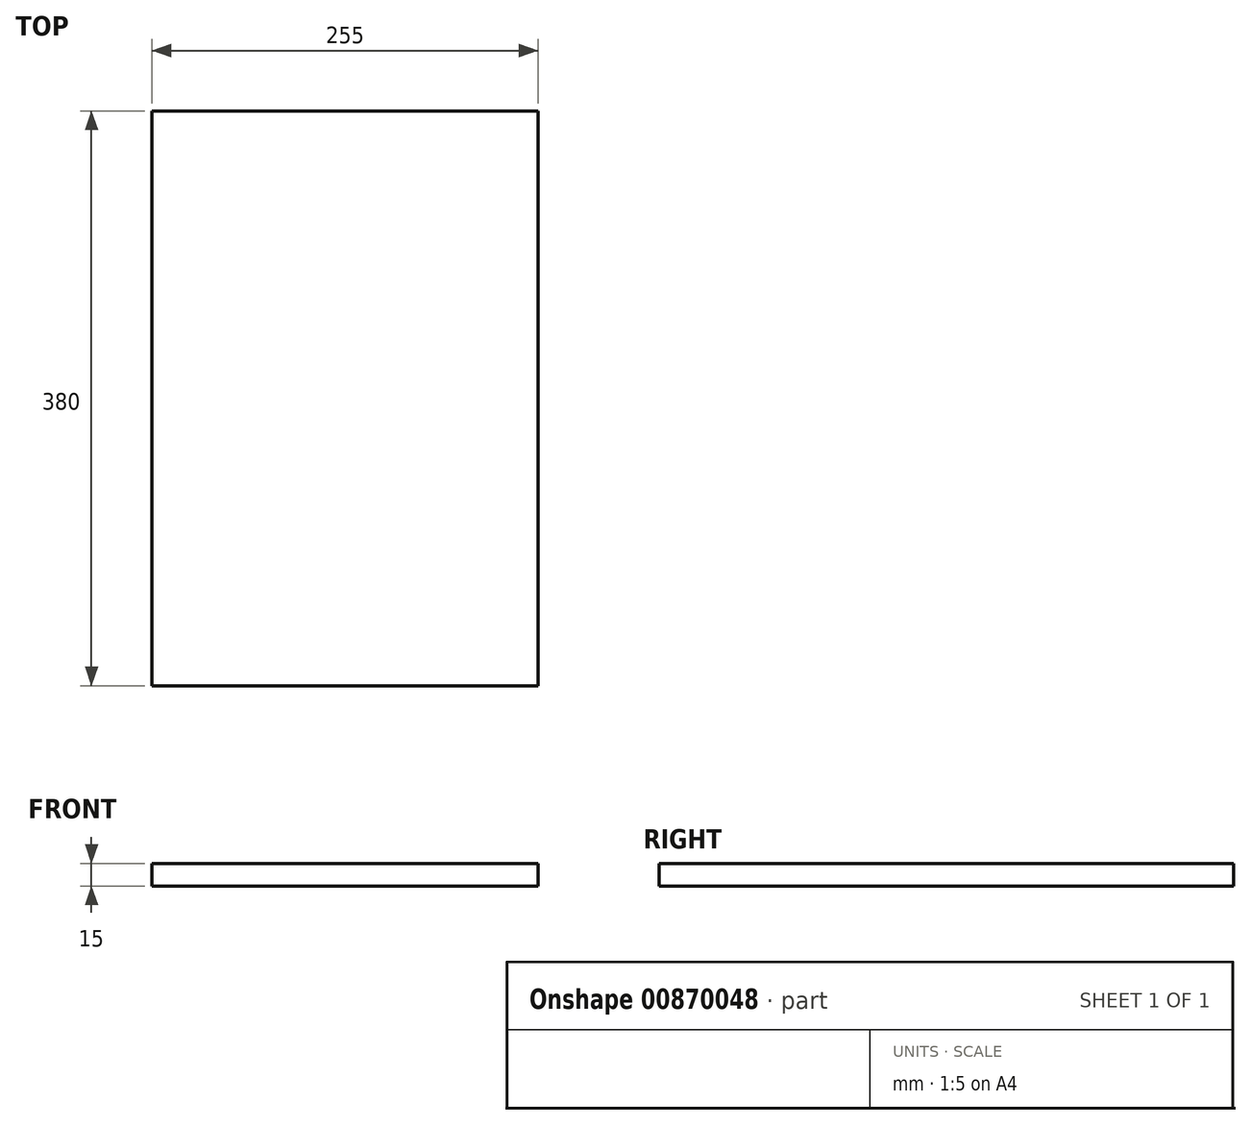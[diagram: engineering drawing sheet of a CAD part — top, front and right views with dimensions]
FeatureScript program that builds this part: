
annotation { "Feature Type Name" : "Feature", "Feature Type Description" : "" }
export const myFeature = defineFeature(function(context is Context, id is Id, definition is map)
    precondition{}
    {
        {
            var Q0;
            Q0=qCreatedBy(makeId("Front.planeOp"),FACE);
            var sketch = newSketch(context, id + "F0", { "sketchPlane" : qUnion([Q0])});
            skLineSegment(sketch, "E0.bottom", {"start": v(0, 15) * mm, "end": v(255, 15) * mm});
            skLineSegment(sketch, "E0.top", {"start": v(0, 0) * mm, "end": v(255, 0) * mm});
            skLineSegment(sketch, "E0.left", {"start": v(0, 15) * mm, "end": v(0, 0) * mm});
            skLineSegment(sketch, "E0.right", {"start": v(255, 15) * mm, "end": v(255, 0) * mm});
            skSolve(sketch);
        }
        {
            var Q0;
            Q0=makeQuery(id+"F0.imprint","IMPRINT",FACE,{"disambiguationData":[TD([[makeQuery(id+"F0.imprint","IMPRINT",EDGE,{"derivedFrom":sQuery(id+"F0.wireOp",EDGE,"E0.bottom")}),-1.0]])]});
            extrude(context, id + "F1", {"entities" : qUnion([Q0]), "depth" : 380 * mm, "offsetDistance" : 25.4 * mm});
        }
    });
